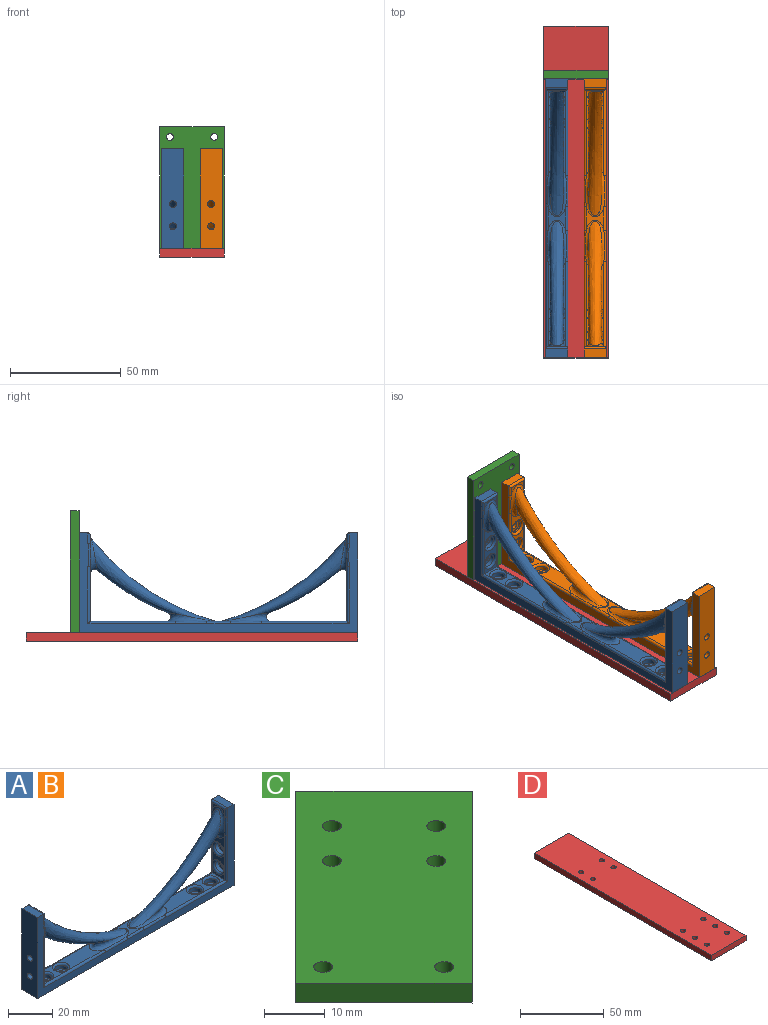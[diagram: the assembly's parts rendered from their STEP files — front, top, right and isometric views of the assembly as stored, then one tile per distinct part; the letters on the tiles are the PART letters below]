
ASSEMBLY  parts=4 mates=3
PART A: 76 faces, bbox 126x10x45 mm
  f0: plane 24.75x8.01mm, normal (-1,0,0), area 84.2mm2, adj f2,f42,f55,f67,f70,f71
  f1: plane 38.64x8.01mm, normal (0,0,1), area 189.8mm2, adj f3,f43,f45,f58,f74,f75
  f2: plane 38.64x8.01mm, normal (0,0,1), area 189.8mm2, adj f0,f41,f53,f66,f72,f73
  f3: plane 24.75x8.01mm, normal (1,0,0), area 84.2mm2, adj f1,f40,f44,f56,f68,f69
  f4: cylinder r=1.55mm len=3.1mm, axis (1,0,0), area 29.2mm2, adj f17,f39
  f5: cylinder r=1.55mm len=3.1mm, axis (1,0,0), area 29.2mm2, adj f17,f37
  f6: cylinder r=1.55mm len=3.1mm, axis (-1,0,0), area 19.5mm2, adj f20,f35
  f7: cylinder r=1.55mm len=3.1mm, axis (-1,0,0), area 19.5mm2, adj f20,f33
  f8: cylinder r=1.55mm len=3.1mm, axis (0,0,1), area 19.5mm2, adj f16,f31
  f9: cylinder r=1.55mm len=3.1mm, axis (0,0,1), area 19.5mm2, adj f16,f29
  f10: cylinder r=1.55mm len=3.1mm, axis (0,0,1), area 19.5mm2, adj f16,f27
  f11: cylinder r=1.55mm len=3.1mm, axis (0,0,1), area 19.5mm2, adj f16,f25
  f12: plane 10.56x8.01mm, normal (0,0,1), area 33mm2, adj f41,f43,f49,f62
  f13: plane 8.01x3.89mm, normal (1,0,0), area 11.1mm2, adj f40,f48,f50,f52
  f14: plane 126x45mm, normal (0,1,0), area 836.5mm2, adj f16,f17,f18,f20,f21,f44,f45,f46
  f15: plane 126x45mm, normal (0,-1,0), area 836.5mm2, adj f16,f17,f18,f20,f21,f52,f54,f56
  f16: plane 126x10mm, normal (0,0,-1), area 1229.8mm2, adj f8,f9,f10,f11,f14,f15,f17,f20
  f17: plane 45x10mm, normal (-1,0,0), area 434.9mm2, adj f4,f5,f14,f15,f16,f18
  f18: plane 10x4mm, normal (0,0,1), area 40mm2, adj f14,f15,f17,f50
  f19: plane 8.01x3.89mm, normal (-1,0,0), area 11.1mm2, adj f42,f59,f61,f63
  f20: plane 45x10mm, normal (1,0,0), area 434.9mm2, adj f6,f7,f14,f15,f16,f21
  f21: plane 10x4mm, normal (0,0,1), area 40mm2, adj f14,f15,f20,f61
  f22: bspline ~56.33x37.39mm, area 967.3mm2, adj f41,f42
  f23: bspline ~56.33x37.39mm, area 967.3mm2, adj f40,f43
  f24: cylinder r=2.9mm len=5.8mm, axis (0,0,1), area 36.4mm2, adj f25,f74
  f25: plane 5.8x5.8mm, normal (0,0,1), area 18.9mm2, adj f11,f24
  f26: cylinder r=2.9mm len=5.8mm, axis (0,0,1), area 36.4mm2, adj f27,f75
  f27: plane 5.8x5.8mm, normal (0,0,1), area 18.9mm2, adj f10,f26
  f28: cylinder r=2.9mm len=5.8mm, axis (0,0,1), area 36.4mm2, adj f29,f72
  f29: plane 5.8x5.8mm, normal (0,0,1), area 18.9mm2, adj f9,f28
  f30: cylinder r=2.9mm len=5.8mm, axis (0,0,1), area 36.4mm2, adj f31,f73
  f31: plane 5.8x5.8mm, normal (0,0,1), area 18.9mm2, adj f8,f30
  f32: cylinder r=2.9mm len=5.8mm, axis (-1,0,0), area 36.4mm2, adj f33,f71
  f33: plane 5.8x5.8mm, normal (-1,0,0), area 18.9mm2, adj f7,f32
  f34: cylinder r=2.9mm len=5.8mm, axis (-1,0,0), area 36.4mm2, adj f35,f70
  f35: plane 5.8x5.8mm, normal (-1,0,0), area 18.9mm2, adj f6,f34
  f36: cylinder r=2.9mm len=5.8mm, axis (1,0,0), area 18.2mm2, adj f37,f69
  f37: plane 5.8x5.8mm, normal (1,0,0), area 18.9mm2, adj f5,f36
  f38: cylinder r=2.9mm len=5.8mm, axis (1,0,0), area 18.2mm2, adj f39,f68
  f39: plane 5.8x5.8mm, normal (1,0,0), area 18.9mm2, adj f4,f38
  f40: bspline ~17.15x9.99mm, area 99.1mm2, adj f3,f13,f23,f46,f54
  f41: bspline ~22.8x10mm, area 139.6mm2, adj f2,f12,f22,f51,f64
  f42: bspline ~17.14x10mm, area 108.7mm2, adj f0,f19,f22,f57,f65
  f43: bspline ~22.8x10mm, area 139.6mm2, adj f1,f12,f23,f47,f60
  f44: cylinder r=1mm len=25.75mm, axis (0,0,-1), area 39.7mm2, adj f3,f14,f45,f46
  f45: cylinder r=1mm len=39.64mm, axis (1,0,0), area 61.5mm2, adj f1,f14,f44,f47
  f46: bspline ~12.2x1.16mm, area 13.9mm2, adj f14,f40,f44,f48
  f47: bspline ~15.29x1.12mm, area 18.9mm2, adj f14,f43,f45,f49
  f48: cylinder r=1mm len=4.89mm, axis (0,0,-1), area 6.9mm2, adj f13,f14,f46,f50
  f49: cylinder r=1mm len=10.55mm, axis (1,0,0), area 16.6mm2, adj f12,f14,f47,f51
  f50: cylinder r=1mm len=10mm, axis (0,-1,0), area 14.1mm2, adj f13,f18,f48,f52
  f51: bspline ~16.05x1.13mm, area 18.9mm2, adj f14,f41,f49,f53
  f52: cylinder r=1mm len=4.89mm, axis (0,0,1), area 6.9mm2, adj f13,f15,f50,f54
  f53: cylinder r=1mm len=39.64mm, axis (1,0,0), area 61.5mm2, adj f2,f14,f51,f55
  f54: bspline ~11.8x1.13mm, area 13.9mm2, adj f15,f40,f52,f56
  f55: cylinder r=1mm len=25.75mm, axis (0,0,1), area 39.7mm2, adj f0,f14,f53,f57
  f56: cylinder r=1mm len=25.75mm, axis (0,0,1), area 39.7mm2, adj f3,f15,f54,f58
  f57: bspline ~12.2x1.16mm, area 13.9mm2, adj f14,f42,f55,f59
  f58: cylinder r=1mm len=39.64mm, axis (-1,0,0), area 61.5mm2, adj f1,f15,f56,f60
  f59: cylinder r=1mm len=4.89mm, axis (0,0,1), area 6.9mm2, adj f14,f19,f57,f61
  f60: bspline ~15.29x1.12mm, area 18.9mm2, adj f15,f43,f58,f62
  f61: cylinder r=1mm len=10mm, axis (0,1,0), area 14.1mm2, adj f19,f21,f59,f63
  f62: cylinder r=1mm len=10.55mm, axis (-1,0,0), area 16.6mm2, adj f12,f15,f60,f64
  f63: cylinder r=1mm len=4.89mm, axis (0,0,-1), area 6.9mm2, adj f15,f19,f61,f65
  f64: bspline ~15.29x1.12mm, area 18.9mm2, adj f15,f41,f62,f66
  f65: bspline ~11.23x1.11mm, area 13.9mm2, adj f15,f42,f63,f67
  f66: cylinder r=1mm len=39.64mm, axis (-1,0,0), area 61.5mm2, adj f2,f15,f64,f67
  f67: cylinder r=1mm len=25.75mm, axis (0,0,-1), area 39.7mm2, adj f0,f15,f65,f66
  f68: torus R=3.9mm, axis (1,0,0), area 32.2mm2, adj f3,f38
  f69: torus R=3.9mm, axis (1,0,0), area 32.2mm2, adj f3,f36
  f70: torus R=3.9mm, axis (1,0,0), area 32.2mm2, adj f0,f34
  f71: torus R=3.9mm, axis (1,0,0), area 32.2mm2, adj f0,f32
  f72: torus R=3.9mm, axis (0,0,1), area 32.2mm2, adj f2,f28
  f73: torus R=3.9mm, axis (0,0,1), area 32.2mm2, adj f2,f30
  f74: torus R=3.9mm, axis (0,0,1), area 32.2mm2, adj f1,f24
  f75: torus R=3.9mm, axis (0,0,1), area 32.2mm2, adj f1,f26
PART B: same geometry as A
PART C: 12 faces, bbox 59.6x59.5x4 mm
  f0: plane 20.7x20.64mm, normal (-0.71,-0.71,0), area 116.9mm2, adj f1,f7,f10,f11
  f1: plane 38.95x38.83mm, normal (0.71,-0.71,0), area 220mm2, adj f0,f2,f10,f11
  f2: plane 20.7x20.64mm, normal (0.71,0.71,0), area 116.9mm2, adj f1,f7,f10,f11
  f3: cylinder r=1.55mm len=4mm, axis (0,0,-1), area 39mm2, adj f10,f11
  f4: cylinder r=1.55mm len=4mm, axis (0,0,-1), area 39mm2, adj f10,f11
  f5: cylinder r=1.55mm len=4mm, axis (0,0,-1), area 39mm2, adj f10,f11
  f6: cylinder r=1.55mm len=4mm, axis (0,0,-1), area 39mm2, adj f10,f11
  f7: plane 38.95x38.83mm, normal (-0.71,0.71,0), area 220mm2, adj f0,f2,f10,f11
  f8: cylinder r=1.55mm len=4mm, axis (0,0,-1), area 39mm2, adj f10,f11
  f9: cylinder r=1.55mm len=4mm, axis (0,0,-1), area 39mm2, adj f10,f11
  f10: plane 59.59x59.54mm, normal (0,0,1), area 1562.7mm2, adj f0,f1,f2,f3,f4,f5,f6,f7
  f11: plane 59.59x59.54mm, normal (0,0,-1), area 1562.7mm2, adj f0,f1,f2,f3,f4,f5,f6,f7
PART D: 16 faces, bbox 29.2x150x4 mm
  f0: plane 150x4mm, normal (-1,0,0), area 600mm2, adj f1,f13,f14,f15
  f1: plane 29.24x4mm, normal (0,-1,0), area 116.9mm2, adj f0,f2,f14,f15
  f2: plane 150x4mm, normal (1,0,0), area 600mm2, adj f1,f13,f14,f15
  f3: cylinder r=1.55mm len=4mm, axis (0,0,-1), area 39mm2, adj f14,f15
  f4: cylinder r=1.55mm len=4mm, axis (0,0,-1), area 39mm2, adj f14,f15
  f5: cylinder r=1.55mm len=4mm, axis (0,0,-1), area 39mm2, adj f14,f15
  f6: cylinder r=1.55mm len=4mm, axis (0,0,-1), area 39mm2, adj f14,f15
  f7: cylinder r=1.55mm len=4mm, axis (0,0,-1), area 39mm2, adj f14,f15
  f8: cylinder r=1.55mm len=4mm, axis (0,0,-1), area 39mm2, adj f14,f15
  f9: cylinder r=1.55mm len=4mm, axis (0,0,-1), area 39mm2, adj f14,f15
  f10: cylinder r=1.55mm len=4mm, axis (0,0,-1), area 39mm2, adj f14,f15
  f11: cylinder r=1.55mm len=4mm, axis (0,0,-1), area 39mm2, adj f14,f15
  f12: cylinder r=1.55mm len=4mm, axis (0,0,-1), area 39mm2, adj f14,f15
  f13: plane 29.24x4mm, normal (0,1,0), area 116.9mm2, adj f0,f2,f14,f15
  f14: plane 150x29.24mm, normal (0,0,1), area 4309.8mm2, adj f0,f1,f2,f3,f4,f5,f6,f7
  f15: plane 150x29.24mm, normal (0,0,-1), area 4309.8mm2, adj f0,f1,f2,f3,f4,f5,f6,f7
PLACE A rot(axis=(0,0,1),90deg) t=(-47.04,-116.12,-102.23)mm
PLACE B rot(axis=(0,0,-1),90deg) t=(30.19,9.88,-102.23)mm
PLACE C rot(axis=(0.28,0.68,-0.68),148.5deg) t=(267.6,13.88,-205.08)mm
PLACE D t=(-190.54,288.88,-106.23)mm
MATE fastened B.f8 <-> D.f8  axis (0,0,-1) through (0.19,-106.12,-102.23)mm
MATE fastened A.f11 <-> D.f7  axis (0,0,-1) through (-17.04,-106.12,-102.23)mm
MATE fastened C.f2 <-> D.f14  axis (0,0,-1) through (-8.43,13.88,-102.23)mm
